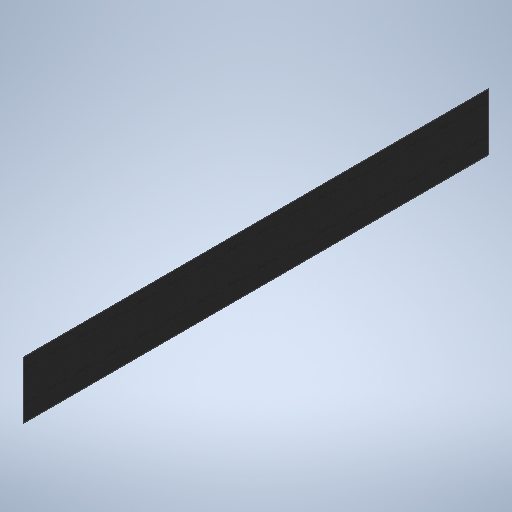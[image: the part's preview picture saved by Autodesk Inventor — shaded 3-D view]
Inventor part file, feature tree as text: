
AUTODESK INVENTOR PART (.ipt)
format: ipt  version: 2025.1 (Build 291241020, 241B)  size: 256,000 bytes
history: native  units: in
note: dims shown in document units (in); Inventor stores cm internally (conversion verified against a paired STEP export)
features: extrude x1, sketch x1
ambient origin geometry x8: Origin, YZ Plane, XZ Plane, XY Plane, X Axis, Y Axis, Z Axis, Center Point
bodies: Solid1 (feature_tree)
feature tree (2):
  extrude  "Extrusion1"  Depth=292.513in
  sketch  "Sketch1"  dims[d2=0.125in d3=0.0in d4=292.513in d5=36.0in]
